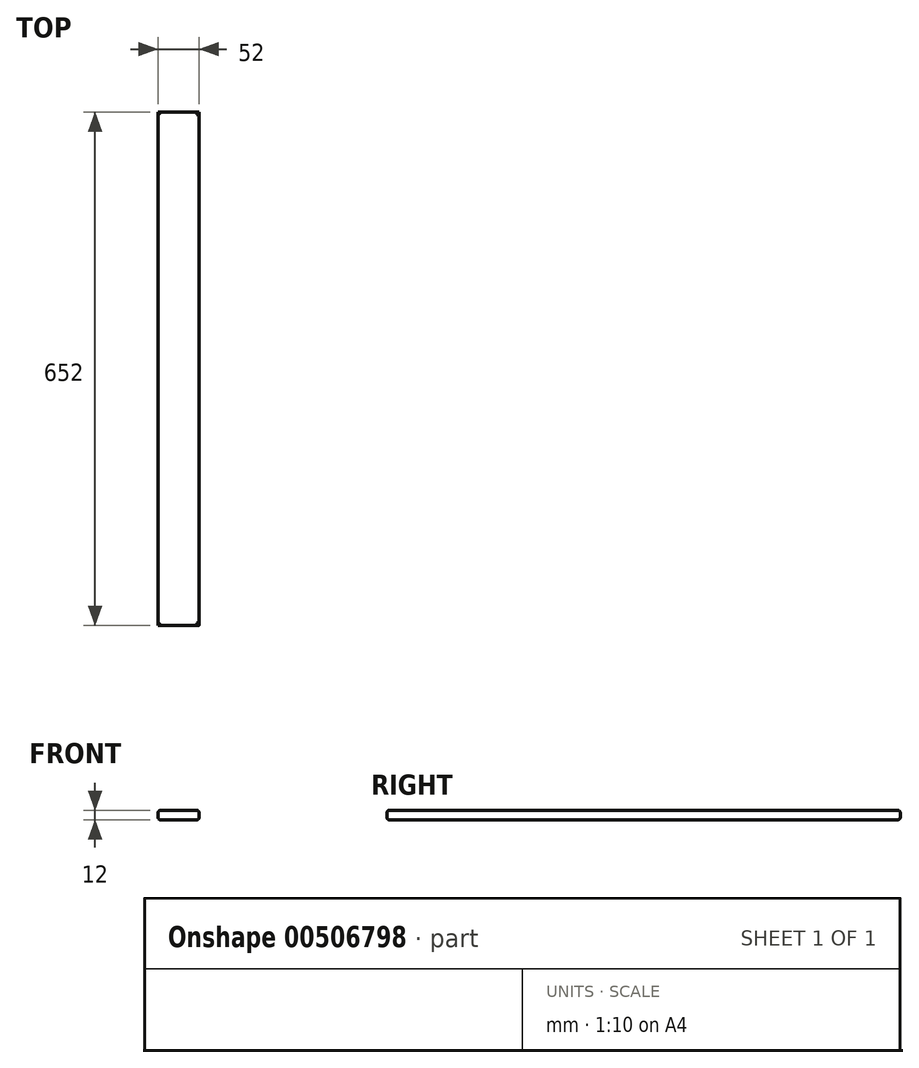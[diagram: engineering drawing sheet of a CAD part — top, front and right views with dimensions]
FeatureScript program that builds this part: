
annotation { "Feature Type Name" : "Feature", "Feature Type Description" : "" }
export const myFeature = defineFeature(function(context is Context, id is Id, definition is map)
    precondition{}
    {
        {
            var Q0;
            Q0=qCreatedBy(makeId("Front.planeOp"),FACE);
            var sketch = newSketch(context, id + "F0", { "sketchPlane" : qUnion([Q0])});
            skLineSegment(sketch, "E0.bottom", {"start": v(-127.13, 29.2) * mm, "end": v(-75.13, 29.2) * mm});
            skLineSegment(sketch, "E0.top", {"start": v(-127.13, 17.2) * mm, "end": v(-75.13, 17.2) * mm});
            skLineSegment(sketch, "E0.left", {"start": v(-127.13, 29.2) * mm, "end": v(-127.13, 17.2) * mm});
            skLineSegment(sketch, "E0.right", {"start": v(-75.13, 29.2) * mm, "end": v(-75.13, 17.2) * mm});
            skSolve(sketch);
        }
        {
            var Q0;
            Q0=makeQuery(id+"F0.imprint","IMPRINT",FACE,{"disambiguationData":[TD([[makeQuery(id+"F0.imprint","IMPRINT",EDGE,{"derivedFrom":sQuery(id+"F0.wireOp",EDGE,"E0.bottom")}),-1.0]])]});
            extrude(context, id + "F1", {"entities" : qUnion([Q0]), "depth" : 652 * mm});
        }
        {
            var Q0;
            Q0=makeQuery(id+"F1.opExtrude","SWEPT_FACE",FACE,{"disambiguationData":[OSD([sQuery(id+"F0.wireOp",EDGE,"E0.bottom")])]});
            var Q1;
            Q1=makeQuery(id+"F1.opExtrude","SWEPT_FACE",FACE,{"disambiguationData":[OSD([sQuery(id+"F0.wireOp",EDGE,"E0.top")])]});
            fillet(context, id + "F2", {"entities" : qUnion([Q0, Q1]), "radius" : 3 * mm, "tangentPropagation" : true, "allowEdgeOverflow" : false});
        }
        {
            var Q0;
            Q0=makeQuery(id+"F1.opExtrude","SWEPT_FACE",FACE,{"disambiguationData":[OSD([sQuery(id+"F0.wireOp",EDGE,"E0.bottom")])]});
            var sketch = newSketch(context, id + "F3", { "sketchPlane" : qUnion([Q0])});
            skLineSegment(sketch, "E1", {"start": v(-124.13, -3) * mm, "end": v(-107.13, -3) * mm});
            skLineSegment(sketch, "E2", {"start": v(-107.13, -3) * mm, "end": v(-107.13, -300) * mm});
            skLineSegment(sketch, "E3", {"start": v(-107.13, -326) * mm, "end": v(-107.13, -649) * mm});
            skLineSegment(sketch, "E4", {"start": v(-107.13, -300) * mm, "end": v(-107.13, -326) * mm});
            skSolve(sketch);
        }
    });
